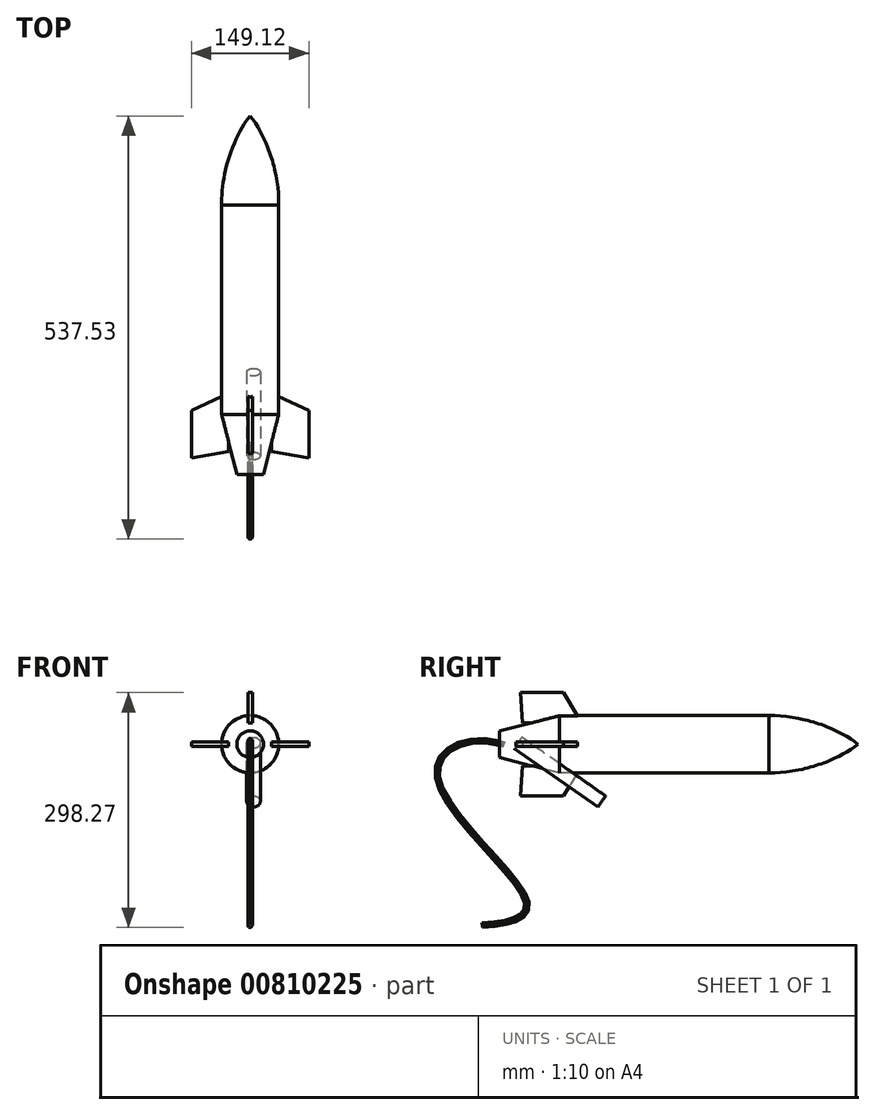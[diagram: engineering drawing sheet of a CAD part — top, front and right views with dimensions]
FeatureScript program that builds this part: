
annotation { "Feature Type Name" : "Feature", "Feature Type Description" : "" }
export const myFeature = defineFeature(function(context is Context, id is Id, definition is map)
    precondition{}
    {
        {
            var Q0;
            Q0=qCreatedBy(makeId("Top.planeOp"),FACE);
            var sketch = newSketch(context, id + "F0", { "sketchPlane" : qUnion([Q0])});
            skFitSpline(sketch, "E0", {"points": [v(0, 330.16) * mm, v(-27.28, 276.17) * mm, v(-36.3, 217.04) * mm], "startDerivative": vector(-58.06, -66.28) * mm, "endDerivative": vector(3.28, -91.69) * mm});
            skLineSegment(sketch, "E1", {"start": v(-36.3, 217.04) * mm, "end": v(-36.3, -48.98) * mm});
            skLineSegment(sketch, "E2", {"start": v(-16.93, -125.22) * mm, "end": v(0, -125.22) * mm});
            skLineSegment(sketch, "E3", {"start": v(0, -170.06) * mm, "end": v(0, 265.95) * mm, "construction": true});
            skLineSegment(sketch, "E4", {"start": v(0, 330.16) * mm, "end": v(0, -125.22) * mm});
            skLineSegment(sketch, "E5", {"start": v(-36.3, -48.98) * mm, "end": v(-16.93, -125.22) * mm});
            skSolve(sketch);
        }
        {
            var Q0;
            Q0 = qSketchRegion(id + "F0", true);
            var Q1;
            Q1=sQuery(id+"F0.wireOp",EDGE,"E3");
            revolve(context, id + "F1", {"surfaceOperationType" : NewSurfaceOperationType.NEW, "entities" : qUnion([Q0]), "axis" : qUnion([Q1]), "revolveType" : RevolveType.FULL});
        }
        {
            var Q0;
            Q0=qCreatedBy(makeId("Right.planeOp"),FACE);
            var sketch = newSketch(context, id + "F2", { "sketchPlane" : qUnion([Q0])});
            skLineSegment(sketch, "E6", {"start": v(-21.18, -27.33) * mm, "end": v(-43.78, -65.46) * mm});
            skLineSegment(sketch, "E7", {"start": v(-43.78, -65.46) * mm, "end": v(-98.8, -65.46) * mm});
            skLineSegment(sketch, "E8", {"start": v(-98.8, -65.46) * mm, "end": v(-96.16, -27.28) * mm});
            skLineSegment(sketch, "E9", {"start": v(-96.16, -27.28) * mm, "end": v(-21.18, -27.33) * mm});
            skLineSegment(sketch, "E10.MirrorCS", {"start": v(-21.18, 27.33) * mm, "end": v(-43.78, 65.46) * mm});
            skLineSegment(sketch, "E11.MirrorCS", {"start": v(-96.16, 27.28) * mm, "end": v(-21.18, 27.33) * mm});
            skLineSegment(sketch, "E12.MirrorCS", {"start": v(-43.78, 65.46) * mm, "end": v(-98.8, 65.46) * mm});
            skLineSegment(sketch, "E13.MirrorCS", {"start": v(-98.8, 65.46) * mm, "end": v(-96.16, 27.28) * mm});
            skSolve(sketch);
        }
        {
            var Q0;
            Q0 = qSketchRegion(id + "F2", true);
            extrude(context, id + "F3", {"entities" : qUnion([Q0]), "operationType" : NewBodyOperationType.ADD, "depth" : 3 * mm, "offsetDistance" : 25 * mm, "hasSecondDirection" : true, "secondDirectionOppositeDirection" : true, "secondDirectionDepth" : 3 * mm});
        }
        {
            var Q0;
            Q0=qCreatedBy(makeId("Top.planeOp"),FACE);
            var sketch = newSketch(context, id + "F4", { "sketchPlane" : qUnion([Q0])});
            skLineSegment(sketch, "E14", {"start": v(-27.2, -21.83) * mm, "end": v(-74.56, -43.84) * mm});
            skLineSegment(sketch, "E15", {"start": v(-74.56, -43.84) * mm, "end": v(-74.56, -104.5) * mm});
            skLineSegment(sketch, "E16", {"start": v(-74.56, -104.5) * mm, "end": v(-27.2, -96.29) * mm});
            skLineSegment(sketch, "E17", {"start": v(-27.2, -96.29) * mm, "end": v(-27.2, -21.83) * mm});
            skLineSegment(sketch, "E18.MirrorCS", {"start": v(27.2, -96.29) * mm, "end": v(27.2, -21.83) * mm});
            skLineSegment(sketch, "E19.MirrorCS", {"start": v(27.2, -21.83) * mm, "end": v(74.56, -43.84) * mm});
            skLineSegment(sketch, "E20.MirrorCS", {"start": v(74.56, -43.84) * mm, "end": v(74.56, -104.5) * mm});
            skLineSegment(sketch, "E21.MirrorCS", {"start": v(74.56, -104.5) * mm, "end": v(27.2, -96.29) * mm});
            skSolve(sketch);
        }
        {
            var Q0;
            Q0 = qSketchRegion(id + "F4", true);
            extrude(context, id + "F5", {"entities" : qUnion([Q0]), "operationType" : NewBodyOperationType.ADD, "depth" : 3 * mm, "offsetDistance" : 25 * mm, "hasSecondDirection" : true, "secondDirectionOppositeDirection" : true, "secondDirectionDepth" : 3 * mm});
        }
        {
            var Q0;
            Q0=qCreatedBy(makeId("Front.planeOp"),FACE);
            cPlane(context, id + "F6", {"entities" : qUnion([Q0]), "cplaneType" : CPlaneType.OFFSET, "offset" : 136 * mm, "width" : 150 * mm, "height" : 150 * mm});
        }
        {
            var Q0;
            Q0=qCreatedBy(id+"F6.planeOp",FACE);
            var sketch = newSketch(context, id + "F7", { "sketchPlane" : qUnion([Q0])});
            skLineSegment(sketch, "E22", {"start": v(-246.05, 0) * mm, "end": v(288.5, 0) * mm});
            skSolve(sketch);
        }
        {
            var Q0;
            Q0=qCreatedBy(id+"F6.planeOp",FACE);
            var Q1;
            Q1=sQuery(id+"F7.wireOp",EDGE,"E22");
            cPlane(context, id + "F8", {"entities" : qUnion([Q0, Q1]), "cplaneType" : CPlaneType.LINE_ANGLE, "offset" : 25 * mm, "angle" : 35 * degree, "oppositeDirection" : true, "width" : 150 * mm, "height" : 150 * mm});
        }
        {
            var Q0;
            Q0=qCreatedBy(id+"F8.planeOp",FACE);
            var sketch = newSketch(context, id + "F9", { "sketchPlane" : qUnion([Q0])});
            skCircle(sketch, "E23", {"center": v(-4.27, -56.86) * mm, "radius": 8.6 * mm});
            skSolve(sketch);
        }
        {
            var Q0;
            Q0 = qSketchRegion(id + "F9", true);
            extrude(context, id + "F10", {"entities" : qUnion([Q0]), "depth" : 130 * mm, "offsetDistance" : 25 * mm});
        }
        {
            var Q0;
            Q0=makeQuery(id+"F10.opExtrude","SWEPT_BODY",BODY,{"disambiguationData":[OSD([sQuery(id+"F9.wireOp",EDGE,"E23")])]});
            var Q1;
            Q1=qCreatedBy(id+"F8.planeOp",FACE);
            transform(context, id + "F11", {"entities" : qUnion([Q0]), "transformType" : TransformType.TRANSLATION_DISTANCE, "transformDirection" : qUnion([Q1]), "distance" : 27 * mm, "makeCopy" : false});
        }
        {
            var Q0;
            Q0=qCreatedBy(makeId("Right.planeOp"),FACE);
            var sketch = newSketch(context, id + "F12", { "sketchPlane" : qUnion([Q0])});
            skFitSpline(sketch, "E24", {"points": [v(-119.73, 0) * mm, v(-204.42, -39.47) * mm, v(-90.4, -203.14) * mm, v(-147.02, -230) * mm], "startDerivative": vector(-439.56, 134.61) * mm, "endDerivative": vector(-355.23, -21.53) * mm});
            skSolve(sketch);
        }
        {
            var Q0;
            Q0=sQuery(id+"F12.wireOp",EDGE,"E24");
            var Q1;
            Q1=sQuery(id+"F12.wireOp",VERTEX,"E24.end");
            cPlane(context, id + "F13", {"entities" : qUnion([Q0, Q1]), "cplaneType" : CPlaneType.CURVE_POINT, "offset" : 25 * mm, "width" : 150 * mm, "height" : 150 * mm});
        }
        {
            var Q0;
            Q0=qCreatedBy(id+"F13.planeOp",FACE);
            var sketch = newSketch(context, id + "F14", { "sketchPlane" : qUnion([Q0])});
            skCircle(sketch, "E25.cCircle", {"center": v(0, -220.71) * mm, "radius": 2.62 * mm, "construction": true});
            skLineSegment(sketch, "E25.0", {"start": v(-1.82, -223.13) * mm, "end": v(-3, -220.34) * mm});
            skLineSegment(sketch, "E25.1", {"start": v(-3, -220.34) * mm, "end": v(-1.18, -217.92) * mm});
            skLineSegment(sketch, "E25.2", {"start": v(-1.18, -217.92) * mm, "end": v(1.82, -218.3) * mm});
            skLineSegment(sketch, "E25.3", {"start": v(1.82, -218.3) * mm, "end": v(3, -221.08) * mm});
            skLineSegment(sketch, "E25.4", {"start": v(3, -221.08) * mm, "end": v(1.18, -223.5) * mm});
            skLineSegment(sketch, "E25.5", {"start": v(1.18, -223.5) * mm, "end": v(-1.82, -223.13) * mm});
            skPoint(sketch, "E25.0.midPoint", {"position": v(-2.41, -221.73) * mm});
            skSolve(sketch);
        }
        {
            var Q0;
            Q0=makeQuery(id+"F14.imprint","IMPRINT",FACE,{"disambiguationData":[TD([[makeQuery(id+"F14.imprint","IMPRINT",EDGE,{"derivedFrom":sQuery(id+"F14.wireOp",EDGE,"E25.0")}),-1.0]])]});
            var Q1;
            Q1=sQuery(id+"F12.wireOp",EDGE,"E24");
            sweep(context, id + "F15", {"profiles" : qUnion([Q0]), "path" : qUnion([Q1])});
        }
        {
            var Q0;
            Q0=qCreatedBy(makeId("Right.planeOp"),FACE);
            var sketch = newSketch(context, id + "F16", { "sketchPlane" : qUnion([Q0])});
            skLineSegment(sketch, "E26", {"start": v(-149.84, -229.78) * mm, "end": v(43.72, -392.56) * mm});
            skSolve(sketch);
        }
    });
